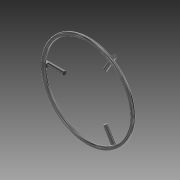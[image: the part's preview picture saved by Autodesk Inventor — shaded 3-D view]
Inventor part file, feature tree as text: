
AUTODESK INVENTOR PART (.ipt)
format: ipt  version: 2014 (Build 180170000, 170)  size: 157,184 bytes
history: native  units: mm
features: sketch x4, extrude x3, plane x2, revolve x1, other x1, pattern_circular x1
ambient origin geometry x8: Origin, YZ Plane, XZ Plane, XY Plane, X Axis, Y Axis, Z Axis, Center Point
bodies: Solid1 (feature_tree)
feature tree (12):
  revolve  "Revolution1"  [1 undecoded]
  plane  "Work Plane1"
  extrude  "Extrusion1"  TaperAngle=90.0deg  [1 undecoded]
  extrude  "Extrusion2"  Depth=6.0mm
  other  "Work Axis1"
  pattern_circular  "Circular Pattern1"  [2 undecoded]
  plane  "Work Plane2"
  extrude  "Extrusion3"  Depth=6.0mm
  sketch  "Sketch1"  dims[d0=6.0mm d1=148.0mm]
  sketch  "Sketch2"  dims[d2=10.0mm d3=90.0deg]
  sketch  "Sketch3"  dims[d4=-3.0mm d5=6.0mm]
  sketch  "Sketch4"  dims[d6=6.0mm d7=6.0mm d8=6.0mm d9=6.0mm d10=0.0mm d11=6.0mm d12=26.0mm d13=0.0mm d14=30.0mm d15=360.0deg d17=9.0mm d18=91.0mm d19=74.0mm d20=26.0mm d21=0.0mm]
note: 4 required parameter values undecoded (feature->parameter linkage not recoverable at this tier; creation-order binding heuristic only, values carry confidence <= 0.55)